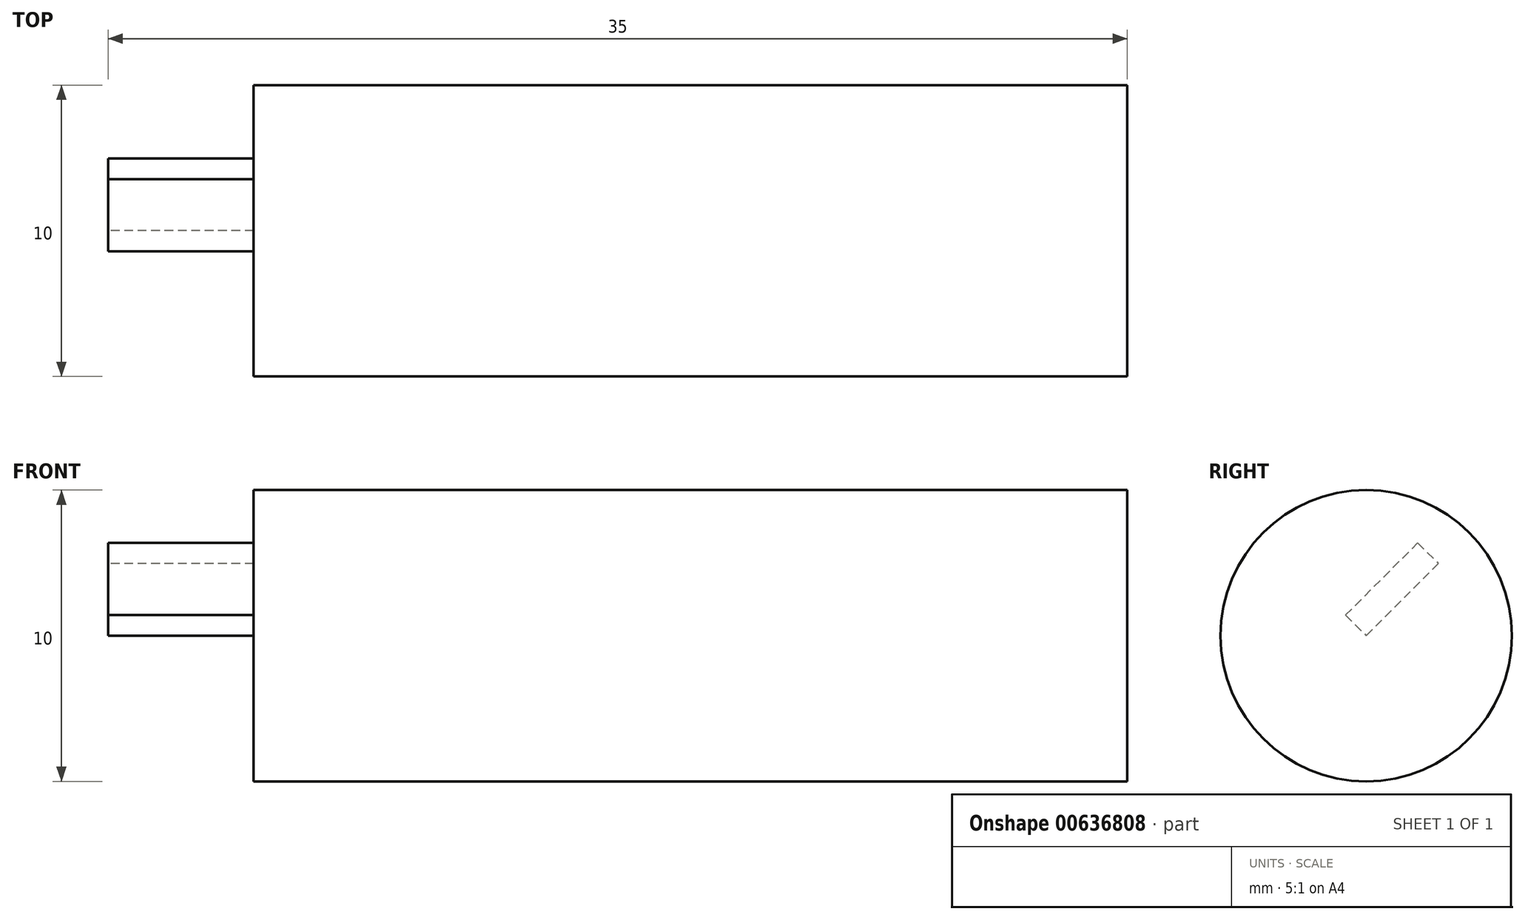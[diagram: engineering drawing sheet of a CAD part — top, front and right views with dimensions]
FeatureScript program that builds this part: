
annotation { "Feature Type Name" : "Feature", "Feature Type Description" : "" }
export const myFeature = defineFeature(function(context is Context, id is Id, definition is map)
    precondition{}
    {
        {
            var Q0;
            Q0=qCreatedBy(makeId("Right.planeOp"),FACE);
            var sketch = newSketch(context, id + "F0", { "sketchPlane" : qUnion([Q0])});
            skCircle(sketch, "E0.0", {"center": v(0, 0) * mm, "radius": 5 * mm});
            skLineSegment(sketch, "E1", {"start": v(0, 0) * mm, "end": v(2.48, 2.48) * mm});
            skSolve(sketch);
        }
        {
            var Q0;
            Q0=makeQuery(id+"F0.imprint","IMPRINT",FACE,{"disambiguationData":[TD([[makeQuery(id+"F0.imprint","IMPRINT",EDGE,{"derivedFrom":sQuery(id+"F0.wireOp",EDGE,"E0.0")}),1.0]])]});
            extrude(context, id + "F1", {"entities" : qUnion([Q0]), "depth" : 30 * mm, "offsetDistance" : 25 * mm});
        }
        {
            var Q0;
            Q0=sQuery(id+"F0.wireOp",EDGE,"E1");
            extrude(context, id + "F2", {"bodyType" : ExtendedToolBodyType.SURFACE, "surfaceEntities" : qUnion([Q0]), "oppositeDirection" : true, "depth" : 5 * mm, "offsetDistance" : 25 * mm});
        }
        {
            var Q0;
            Q0=makeQuery(id+"F2.opExtrude","SWEPT_FACE",FACE,{"disambiguationData":[OSD([sQuery(id+"F0.wireOp",EDGE,"E1")])]});
            extrude(context, id + "F3", {"entities" : qUnion([Q0]), "operationType" : NewBodyOperationType.ADD, "depth" : 1 * mm, "offsetDistance" : 25 * mm});
        }
    });
